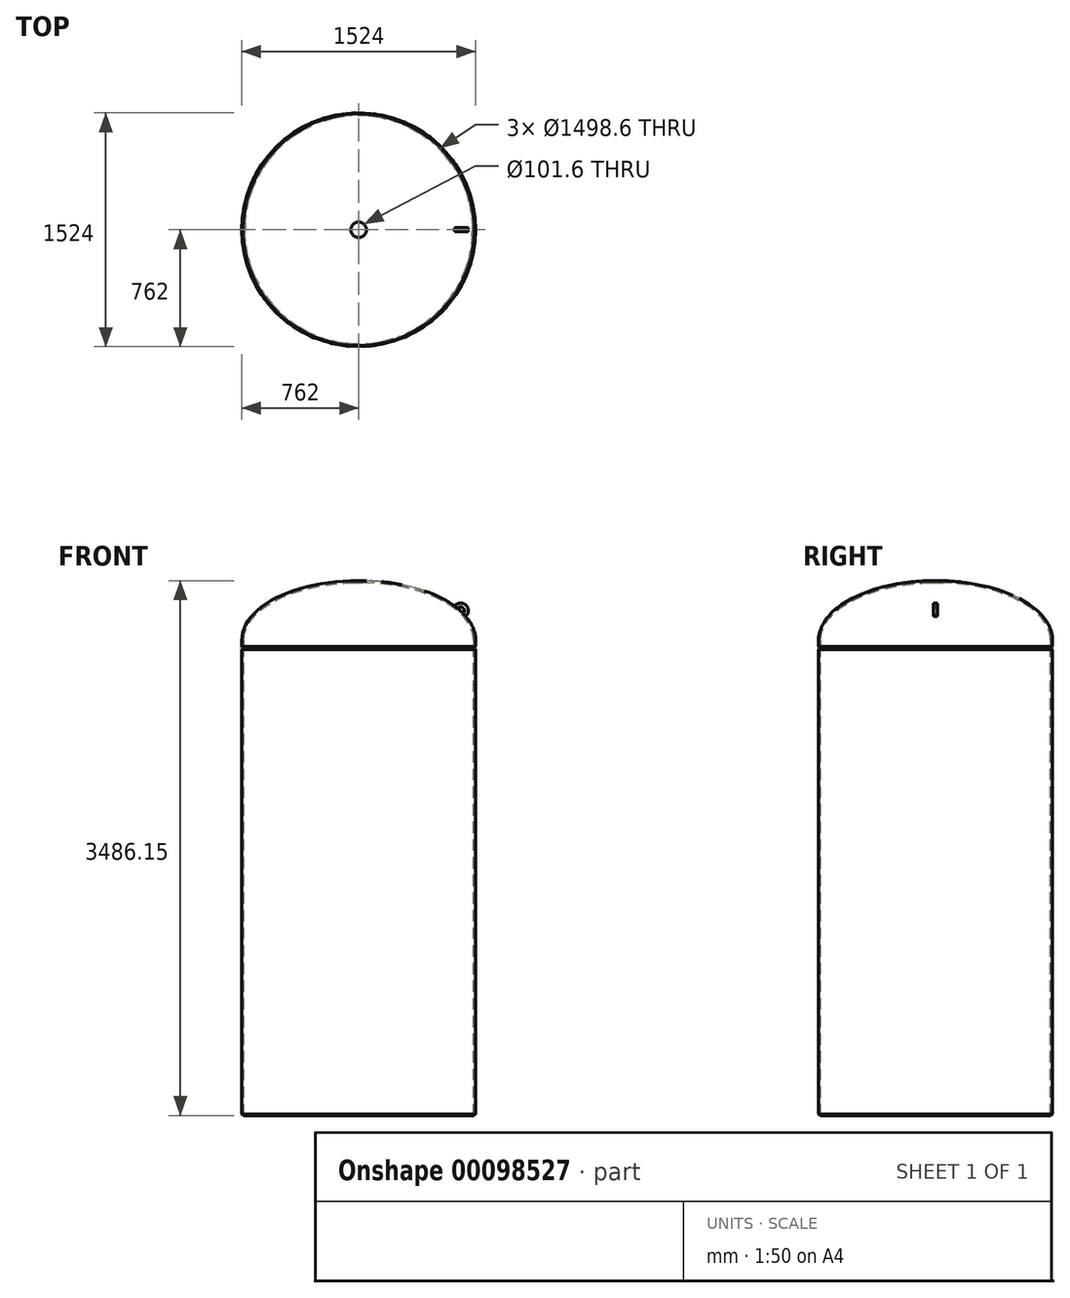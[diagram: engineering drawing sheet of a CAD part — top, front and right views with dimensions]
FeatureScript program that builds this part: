
annotation { "Feature Type Name" : "Feature", "Feature Type Description" : "" }
export const myFeature = defineFeature(function(context is Context, id is Id, definition is map)
    precondition{}
    {
        {
            var Q0;
            Q0=qCreatedBy(makeId("Front.planeOp"),FACE);
            var sketch = newSketch(context, id + "F0", { "sketchPlane" : qUnion([Q0])});
            skLineSegment(sketch, "E0", {"start": v(0, 0) * mm, "end": v(749.3, 0) * mm, "construction": true});
            skLineSegment(sketch, "E1", {"start": v(0, 0) * mm, "end": v(0, 50.8) * mm, "construction": true});
            skLineSegment(sketch, "E2", {"start": v(749.3, 0) * mm, "end": v(749.3, 50.8) * mm});
            skEllipticalArc(sketch, "E3", {});
            skLineSegment(sketch, "E4", {"start": v(0, 50.8) * mm, "end": v(0, 425.45) * mm, "construction": true});
            skLineSegment(sketch, "E5", {"start": v(762, 7.33) * mm, "end": v(762, 50.8) * mm});
            skLineSegment(sketch, "E6", {"start": v(0, 425.45) * mm, "end": v(0, 438.15) * mm});
            skEllipticalArc(sketch, "E7", {});
            skLineSegment(sketch, "E8", {"start": v(762, 7.33) * mm, "end": v(762, 241.3) * mm, "construction": true});
            skLineSegment(sketch, "E9", {"start": v(762, 241.3) * mm, "end": v(663.48, 241.3) * mm, "construction": true});
            skArc(sketch, "E10", {"start": v(699.02, 205) * mm, "mid": v(697.62, 278.91) * mm, "end": v(623.92, 273.17) * mm});
            skArc(sketch, "E11", {"start": v(681.83, 223.74) * mm, "mid": v(680.49, 260.16) * mm, "end": v(644.13, 257.75) * mm});
            skLineSegment(sketch, "E12", {"start": v(749.3, 0) * mm, "end": v(762, 7.33) * mm});
            skLineSegment(sketch, "E13", {"start": v(0, 431.8) * mm, "end": v(50.8, 431.8) * mm, "construction": true});
            skLineSegment(sketch, "E14", {"start": v(50.8, 424.59) * mm, "end": v(50.8, 437.29) * mm});
            skLineSegment(sketch, "E15", {"start": v(0, 0) * mm, "end": v(0, -1524) * mm, "construction": true});
            skLineSegment(sketch, "E16", {"start": v(0, -1524) * mm, "end": v(762, -1524) * mm, "construction": true});
            const initialGuessF0  = {"E3": [0, 0.0508, 1, 0, 0.7493, 0.37465, 0, 1.5707963267948966], "E7": [0, 0.0508, 1, 0, 0.762, 0.38735, 0, 1.5707963267948966]};
            skSetInitialGuess(sketch, initialGuessF0);
            skSolve(sketch);
        }
        {
            var Q0;
            {var subQ5=sQuery(id+"F0.wireOp",EDGE,"E2");Q0=makeQuery(id+"F0.imprint","IMPRINT",FACE,{"disambiguationData":[TD([[makeQuery(id+"F0.imprint","IMPRINT",EDGE,{"derivedFrom":subQ5}),-1.0]])]});}
            var Q1;
            Q1=sQuery(id+"F0.wireOp",EDGE,"E4");
            revolve(context, id + "F1", {"entities" : qUnion([Q0]), "axis" : qUnion([Q1]), "revolveType" : RevolveType.FULL});
        }
        {
            var Q0;
            {var subQ0=sQuery(id+"F0.wireOp",EDGE,"E10");Q0=makeQuery(id+"F0.imprint","IMPRINT",FACE,{"disambiguationData":[TD([[makeQuery(id+"F0.imprint","IMPRINT",EDGE,{"derivedFrom":subQ0}),1.0]])]});}
            extrude(context, id + "F2", {"entities" : qUnion([Q0]), "operationType" : NewBodyOperationType.ADD, "depth" : 25.4 * mm, "symmetric" : true});
        }
        {
            var Q0;
            Q0=qCreatedBy(makeId("Front.planeOp"),FACE);
            var sketch = newSketch(context, id + "F3", { "sketchPlane" : qUnion([Q0])});
            skLineSegment(sketch, "E17", {"start": v(0, 0) * mm, "end": v(0, -3048) * mm, "construction": true});
            skLineSegment(sketch, "E18.left", {"start": v(749.3, 0) * mm, "end": v(749.3, -3048) * mm});
            skLineSegment(sketch, "E18.right", {"start": v(762, -9.57) * mm, "end": v(762, -3038.43) * mm});
            skLineSegment(sketch, "E19", {"start": v(749.3, 0) * mm, "end": v(762, -9.57) * mm});
            skLineSegment(sketch, "E20", {"start": v(749.3, -3048) * mm, "end": v(762, -3038.43) * mm});
            skLineSegment(sketch, "E21", {"start": v(0, -3048) * mm, "end": v(749.3, -3048) * mm, "construction": true});
            skSolve(sketch);
        }
        {
            var Q0;
            Q0=makeQuery(id+"F3.imprint","IMPRINT",FACE,{"disambiguationData":[TD([[makeQuery(id+"F3.imprint","IMPRINT",EDGE,{"derivedFrom":sQuery(id+"F3.wireOp",EDGE,"E18.left")}),1.0]])]});
            var Q1;
            Q1=sQuery(id+"F3.wireOp",EDGE,"E17");
            revolve(context, id + "F4", {"entities" : qUnion([Q0]), "axis" : qUnion([Q1]), "revolveType" : RevolveType.FULL});
        }
        {
            var Q0;
            {var subQ0=sQuery(id+"F0.wireOp",EDGE,"E6");Q0=makeQuery(id+"F0.imprint","IMPRINT",FACE,{"disambiguationData":[TD([[makeQuery(id+"F0.imprint","IMPRINT",EDGE,{"derivedFrom":subQ0}),-1.0]])]});}
            var Q1;
            {var subQ5=sQuery(id+"F0.wireOp",EDGE,"E2");Q1=makeQuery(id+"F0.imprint","IMPRINT",FACE,{"disambiguationData":[TD([[makeQuery(id+"F0.imprint","IMPRINT",EDGE,{"derivedFrom":subQ5}),-1.0]])]});}
            var Q2;
            Q2=sQuery(id+"F0.wireOp",EDGE,"E4");
            revolve(context, id + "F5", {"entities" : qUnion([Q0, Q1]), "axis" : qUnion([Q2]), "revolveType" : RevolveType.FULL});
        }
    });
